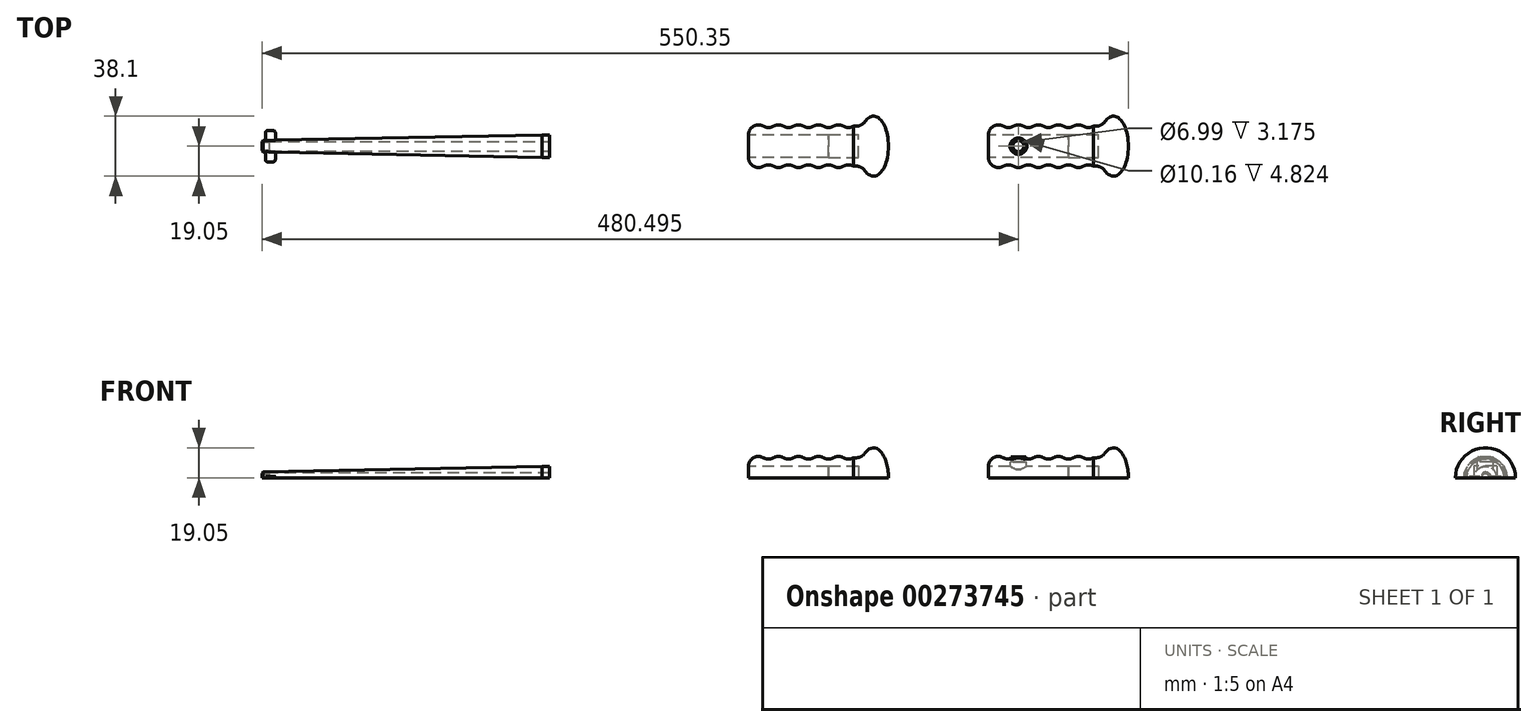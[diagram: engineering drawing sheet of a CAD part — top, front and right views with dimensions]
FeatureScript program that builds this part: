
annotation { "Feature Type Name" : "Feature", "Feature Type Description" : "" }
export const myFeature = defineFeature(function(context is Context, id is Id, definition is map)
    precondition{}
    {
        {
            var Q0;
            Q0=qCreatedBy(makeId("Top.planeOp"),FACE);
            var sketch = newSketch(context, id + "F0", { "sketchPlane" : qUnion([Q0])});
            skPoint(sketch, "E0.middle", {"position": v(0, 0) * mm});
            skEllipticalArc(sketch, "E1", {});
            skPoint(sketch, "E2.orphan", {"position": v(57.15, -12.7) * mm});
            skPoint(sketch, "E3.orphan", {"position": v(57.15, 12.7) * mm});
            skArc(sketch, "E4.3.0.1", {"start": v(-12.7, 12.7) * mm, "mid": v(-9.52, 11.85) * mm, "end": v(-6.35, 12.7) * mm});
            skArc(sketch, "E4.4.0.0", {"start": v(0, 12.7) * mm, "mid": v(-3.17, 13.55) * mm, "end": v(-6.35, 12.7) * mm});
            skArc(sketch, "E4.4.0.1", {"start": v(0, 12.7) * mm, "mid": v(3.18, 11.85) * mm, "end": v(6.35, 12.7) * mm});
            skArc(sketch, "E4.5.0.0", {"start": v(12.7, 12.7) * mm, "mid": v(9.53, 13.55) * mm, "end": v(6.35, 12.7) * mm});
            skArc(sketch, "E4.5.0.1", {"start": v(12.7, 12.7) * mm, "mid": v(15.88, 11.85) * mm, "end": v(19.05, 12.7) * mm});
            skArc(sketch, "E4.6.0.0", {"start": v(25.4, 12.7) * mm, "mid": v(22.23, 13.55) * mm, "end": v(19.05, 12.7) * mm});
            skArc(sketch, "E4.6.0.1", {"start": v(25.4, 12.7) * mm, "mid": v(28.58, 11.85) * mm, "end": v(31.75, 12.7) * mm});
            skArc(sketch, "E4.7.0.0", {"start": v(38.1, 12.7) * mm, "mid": v(34.93, 13.55) * mm, "end": v(31.75, 12.7) * mm});
            skArc(sketch, "E4.7.0.1", {"start": v(38.1, 12.7) * mm, "mid": v(41.28, 11.85) * mm, "end": v(44.45, 12.7) * mm});
            skLineSegment(sketch, "E5", {"start": v(44.45, 12.7) * mm, "end": v(46.35, 12.7) * mm});
            skPoint(sketch, "E6.visualSharp", {"position": v(50.05, 12.7) * mm});
            skArc(sketch, "E6.filletArc", {"start": v(46.35, 12.7) * mm, "mid": v(49.3, 13.43) * mm, "end": v(51.57, 15.44) * mm});
            skLineSegment(sketch, "E7", {"start": v(-22.22, 0) * mm, "end": v(66.68, 0) * mm});
            skLineSegment(sketch, "E8", {"start": v(-22.22, 0) * mm, "end": v(-22.22, 7.2) * mm});
            skArc(sketch, "E9.converted", {"start": v(-12.7, 12.7) * mm, "mid": v(-19.05, 12.7) * mm, "end": v(-22.23, 7.2) * mm});
            skPoint(sketch, "E10.orphan", {"position": v(-19.05, 12.7) * mm});
            const initialGuessF0  = {"E1": [0.05715, 0, 0, 1, 0.01905, 0.009525, 4.71238898038469, 0.6259709660529879]};
            skSetInitialGuess(sketch, initialGuessF0);
            skSolve(sketch);
        }
        {
            var Q0;
            Q0=makeQuery(id+"F0.imprint","IMPRINT",FACE,{"disambiguationData":[TD([[makeQuery(id+"F0.imprint","IMPRINT",EDGE,{"derivedFrom":sQuery(id+"F0.wireOp",EDGE,"E1")}),1.0]])]});
            var Q1;
            Q1=sQuery(id+"F0.wireOp",EDGE,"E7");
            revolve(context, id + "F1", {"entities" : qUnion([Q0]), "axis" : qUnion([Q1]), "revolveType" : RevolveType.ONE_DIRECTION, "angle" : 180 * degree});
        }
        {
            var Q0;
            Q0=makeQuery(id+"F1.opRevolve","SWEPT_FACE",FACE,{"disambiguationData":[OSD([sQuery(id+"F0.wireOp",EDGE,"E8")])]});
            extrude(context, id + "F2", {"entities" : qUnion([Q0]), "operationType" : NewBodyOperationType.REMOVE, "oppositeDirection" : true, "depth" : 50.8 * mm});
        }
        {
            var Q0;
            Q0=qCreatedBy(makeId("Top.planeOp"),FACE);
            var sketch = newSketch(context, id + "F3", { "sketchPlane" : qUnion([Q0])});
            skLineSegment(sketch, "E11", {"start": v(-52.07, 0) * mm, "end": v(-331.27, 0) * mm, "construction": true});
            skPoint(sketch, "E11.endSnap0", {"position": v(-60.33, 0) * mm});
            skLineSegment(sketch, "E12", {"start": v(-331.27, 2.5) * mm, "end": v(-331.27, 3.57) * mm});
            skLineSegment(sketch, "E13", {"start": v(-331.27, 3.57) * mm, "end": v(-153.5, 7.2) * mm});
            skLineSegment(sketch, "E14.0", {"start": v(-148.43, 7.2) * mm, "end": v(-153.5, 7.2) * mm});
            skLineSegment(sketch, "E15", {"start": v(-331.27, 2.5) * mm, "end": v(-326.27, 2.5) * mm});
            skLineSegment(sketch, "E16", {"start": v(-326.27, 2.5) * mm, "end": v(-326.28, 3) * mm});
            skLineSegment(sketch, "E17", {"start": v(-326.28, 3) * mm, "end": v(-148.43, 3) * mm});
            skPoint(sketch, "E18.orphan", {"position": v(-52.07, 0) * mm});
            skLineSegment(sketch, "E19", {"start": v(-148.43, 7.2) * mm, "end": v(-148.43, 3) * mm});
            skSolve(sketch);
        }
        {
            var Q0;
            {var subQ1=sQuery(id+"F3.wireOp",EDGE,"E13");Q0=makeQuery(id+"F3.imprint","IMPRINT",FACE,{"disambiguationData":[TD([[makeQuery(id+"F3.imprint","IMPRINT",EDGE,{"derivedFrom":subQ1}),-1.0]])]});}
            var Q1;
            Q1=sQuery(id+"F3.wireOp",EDGE,"E11");
            revolve(context, id + "F4", {"entities" : qUnion([Q0]), "axis" : qUnion([Q1]), "revolveType" : RevolveType.ONE_DIRECTION, "oppositeDirection" : true, "angle" : 180 * degree});
        }
        {
            var Q0;
            Q0=makeQuery(id+"F4.opRevolve","SWEPT_EDGE",EDGE,{"disambiguationData":[OSD([sQuery(id+"F3.wireOp",EDGE,"E12"),sQuery(id+"F3.wireOp",EDGE,"E13")])]});
            chamfer(context, id + "F5", {"entities" : qUnion([Q0]), "width" : 0.76 * mm, "tangentPropagation" : true});
        }
        {
            var Q0;
            Q0=makeQuery(id+"F4.opRevolve","CAP_FACE",FACE,{"disambiguationData":[OSD([sQuery(id+"F3.wireOp",EDGE,"E12"),sQuery(id+"F3.wireOp",EDGE,"E13"),sQuery(id+"F3.wireOp",EDGE,"E14.0"),sQuery(id+"F3.wireOp",EDGE,"E15"),sQuery(id+"F3.wireOp",EDGE,"E16"),sQuery(id+"F3.wireOp",EDGE,"E17"),sQuery(id+"F3.wireOp",EDGE,"E19")])],"isStart":false});
            var sketch = newSketch(context, id + "F6", { "sketchPlane" : qUnion([Q0])});
            skLineSegment(sketch, "E20", {"start": v(-329, 4) * mm, "end": v(-329.08, 8.44) * mm});
            skLineSegment(sketch, "E21", {"start": v(-327.59, 10) * mm, "end": v(-324.29, 10.06) * mm});
            skLineSegment(sketch, "E22", {"start": v(-322.73, 8.57) * mm, "end": v(-322.64, 4.18) * mm});
            skPoint(sketch, "E23.visualSharp", {"position": v(-329.11, 9.96) * mm});
            skArc(sketch, "E23.filletArc", {"start": v(-327.59, 10) * mm, "mid": v(-328.66, 9.52) * mm, "end": v(-329.08, 8.44) * mm});
            skPoint(sketch, "E24.visualSharp", {"position": v(-322.76, 10.1) * mm});
            skArc(sketch, "E24.filletArc", {"start": v(-322.73, 8.57) * mm, "mid": v(-323.2, 9.64) * mm, "end": v(-324.29, 10.06) * mm});
            skPoint(sketch, "E25.visualSharp", {"position": v(-322.63, 3.74) * mm});
            skArc(sketch, "E25.filletArc", {"start": v(-323.02, 3.79) * mm, "mid": v(-322.75, 3.9) * mm, "end": v(-322.64, 4.18) * mm});
            skPoint(sketch, "E26.visualSharp", {"position": v(-328.98, 3.61) * mm});
            skArc(sketch, "E26.filletArc", {"start": v(-329, 4) * mm, "mid": v(-328.87, 3.73) * mm, "end": v(-328.6, 3.62) * mm});
            skLineSegment(sketch, "E27.0", {"start": v(-331.27, 2.5) * mm, "end": v(-326.27, 2.5) * mm});
            skLineSegment(sketch, "E28.0.0", {"start": v(-326.27, 2.5) * mm, "end": v(-326.27, -2.5) * mm, "construction": true});
            skLineSegment(sketch, "E28.0.1", {"start": v(-326.27, 2.5) * mm, "end": v(-331.27, 2.5) * mm, "construction": true});
            skLineSegment(sketch, "E28.0.2", {"start": v(-331.27, -2.5) * mm, "end": v(-331.27, 2.5) * mm, "construction": true});
            skLineSegment(sketch, "E28.0.3", {"start": v(-331.27, -2.5) * mm, "end": v(-326.27, -2.5) * mm, "construction": true});
            skLineSegment(sketch, "E29", {"start": v(-331.27, 0) * mm, "end": v(-326.27, 0) * mm, "construction": true});
            skLineSegment(sketch, "E30.MirrorCS", {"start": v(-329, -4) * mm, "end": v(-329.08, -8.44) * mm});
            skArc(sketch, "E31.MirrorCS", {"start": v(-327.59, -10) * mm, "mid": v(-328.66, -9.52) * mm, "end": v(-329.08, -8.44) * mm});
            skLineSegment(sketch, "E32.MirrorCS", {"start": v(-327.59, -10) * mm, "end": v(-324.29, -10.06) * mm});
            skArc(sketch, "E33.MirrorCS", {"start": v(-322.73, -8.57) * mm, "mid": v(-323.2, -9.64) * mm, "end": v(-324.29, -10.06) * mm});
            skLineSegment(sketch, "E34.MirrorCS", {"start": v(-322.73, -8.57) * mm, "end": v(-322.64, -4.18) * mm});
            skArc(sketch, "E35.MirrorCS", {"start": v(-323.02, -3.79) * mm, "mid": v(-322.75, -3.9) * mm, "end": v(-322.64, -4.18) * mm});
            skArc(sketch, "E36.MirrorCS", {"start": v(-329, -4) * mm, "mid": v(-328.87, -3.73) * mm, "end": v(-328.6, -3.62) * mm});
            skLineSegment(sketch, "E37", {"start": v(-328.6, 3.62) * mm, "end": v(-328.6, 3.37) * mm});
            skLineSegment(sketch, "E38", {"start": v(-328.6, 3.37) * mm, "end": v(-323.02, 3.48) * mm});
            skLineSegment(sketch, "E39", {"start": v(-323.02, 3.48) * mm, "end": v(-323.02, 3.79) * mm});
            skLineSegment(sketch, "E40.MirrorCS", {"start": v(-328.6, 3.37) * mm, "end": v(-334.18, 3.25) * mm});
            skLineSegment(sketch, "E41.MirrorCS", {"start": v(-328.6, -3.62) * mm, "end": v(-328.6, -3.37) * mm});
            skLineSegment(sketch, "E42.MirrorCS", {"start": v(-328.6, -3.37) * mm, "end": v(-323.02, -3.48) * mm});
            skLineSegment(sketch, "E43.MirrorCS", {"start": v(-323.02, -3.48) * mm, "end": v(-323.02, -3.79) * mm});
            skSolve(sketch);
        }
        {
            var Q0;
            Q0=makeQuery(id+"F6.imprint","IMPRINT",FACE,{"disambiguationData":[TD([[makeQuery(id+"F6.imprint","IMPRINT",EDGE,{"derivedFrom":sQuery(id+"F6.wireOp",EDGE,"E30.MirrorCS")}),1.0]])]});
            var Q1;
            Q1=makeQuery(id+"F6.imprint","IMPRINT",FACE,{"disambiguationData":[TD([[makeQuery(id+"F6.imprint","IMPRINT",EDGE,{"derivedFrom":sQuery(id+"F6.wireOp",EDGE,"E20")}),-1.0]])]});
            var Q2;
            {var subQ0=sQuery(id+"F6.wireOp",EDGE,"E37");Q2=makeQuery(id+"F6.imprint","IMPRINT",FACE,{"disambiguationData":[TD([[makeQuery(id+"F6.imprint","IMPRINT",EDGE,{"derivedFrom":subQ0}),1.0]])]});}
            extrude(context, id + "F7", {"entities" : qUnion([Q0, Q1, Q2]), "operationType" : NewBodyOperationType.ADD, "oppositeDirection" : true, "depth" : 0.76 * mm});
        }
        {
            var Q0;
            Q0=makeQuery(id+"F1.opRevolve","CAP_FACE",FACE,{"disambiguationData":[OSD([sQuery(id+"F0.wireOp",EDGE,"E1"),sQuery(id+"F0.wireOp",EDGE,"E4.3.0.1"),sQuery(id+"F0.wireOp",EDGE,"E4.4.0.0"),sQuery(id+"F0.wireOp",EDGE,"E4.4.0.1"),sQuery(id+"F0.wireOp",EDGE,"E4.5.0.0"),sQuery(id+"F0.wireOp",EDGE,"E4.5.0.1"),sQuery(id+"F0.wireOp",EDGE,"E4.6.0.0"),sQuery(id+"F0.wireOp",EDGE,"E4.6.0.1"),sQuery(id+"F0.wireOp",EDGE,"E4.7.0.0"),sQuery(id+"F0.wireOp",EDGE,"E4.7.0.1"),sQuery(id+"F0.wireOp",EDGE,"E5"),sQuery(id+"F0.wireOp",EDGE,"E6.filletArc"),sQuery(id+"F0.wireOp",EDGE,"E7"),sQuery(id+"F0.wireOp",EDGE,"E8"),sQuery(id+"F0.wireOp",EDGE,"E9.converted")])],"isStart":true});
            var sketch = newSketch(context, id + "F8", { "sketchPlane" : qUnion([Q0])});
            skLineSegment(sketch, "E44.bottom", {"start": v(28.58, 7.3) * mm, "end": v(47.63, 7.3) * mm});
            skLineSegment(sketch, "E44.top", {"start": v(28.58, -7.3) * mm, "end": v(47.63, -7.3) * mm});
            skLineSegment(sketch, "E44.left", {"start": v(28.58, 7.3) * mm, "end": v(28.58, -7.3) * mm});
            skLineSegment(sketch, "E44.right", {"start": v(47.63, 7.3) * mm, "end": v(47.63, -7.3) * mm});
            skLineSegment(sketch, "E45.0", {"start": v(28.58, -7.2) * mm, "end": v(28.58, 7.2) * mm, "construction": true});
            skLineSegment(sketch, "E46", {"start": v(28.58, 0) * mm, "end": v(24.41, 0) * mm, "construction": true});
            skPoint(sketch, "E46.endSnap0", {"position": v(28.58, 0) * mm});
            skSolve(sketch);
        }
        {
            var Q0;
            Q0=makeQuery(id+"F8.imprint","IMPRINT",FACE,{"disambiguationData":[TD([[makeQuery(id+"F8.imprint","IMPRINT",EDGE,{"derivedFrom":sQuery(id+"F8.wireOp",EDGE,"E44.bottom")}),-1.0]])]});
            extrude(context, id + "F9", {"entities" : qUnion([Q0]), "operationType" : NewBodyOperationType.REMOVE, "oppositeDirection" : true, "depth" : 7.37 * mm});
        }
        {
            var Q0;
            Q0=makeQuery(id+"F1.opRevolve","SWEPT_BODY",BODY,{"disambiguationData":[OSD([sQuery(id+"F0.wireOp",EDGE,"E1"),sQuery(id+"F0.wireOp",EDGE,"E4.3.0.1"),sQuery(id+"F0.wireOp",EDGE,"E4.4.0.0"),sQuery(id+"F0.wireOp",EDGE,"E4.4.0.1"),sQuery(id+"F0.wireOp",EDGE,"E4.5.0.0"),sQuery(id+"F0.wireOp",EDGE,"E4.5.0.1"),sQuery(id+"F0.wireOp",EDGE,"E4.6.0.0"),sQuery(id+"F0.wireOp",EDGE,"E4.6.0.1"),sQuery(id+"F0.wireOp",EDGE,"E4.7.0.0"),sQuery(id+"F0.wireOp",EDGE,"E4.7.0.1"),sQuery(id+"F0.wireOp",EDGE,"E5"),sQuery(id+"F0.wireOp",EDGE,"E6.filletArc"),sQuery(id+"F0.wireOp",EDGE,"E7"),sQuery(id+"F0.wireOp",EDGE,"E8"),sQuery(id+"F0.wireOp",EDGE,"E9.converted")])]});
            transform(context, id + "F10", {"entities" : qUnion([Q0]), "transformType" : TransformType.TRANSLATION_3D, "dx" : 152.4 * mm, "dy" : 0 * mm, "dz" : 0 * mm, "makeCopy" : true});
        }
        {
            var Q0;
            Q0=makeQuery(id+"F10.opPattern","COPY",FACE,{"derivedFrom":makeQuery(id+"F1.opRevolve","CAP_FACE",FACE,{"disambiguationData":[OSD([sQuery(id+"F0.wireOp",EDGE,"E1"),sQuery(id+"F0.wireOp",EDGE,"E4.3.0.1"),sQuery(id+"F0.wireOp",EDGE,"E4.4.0.0"),sQuery(id+"F0.wireOp",EDGE,"E4.4.0.1"),sQuery(id+"F0.wireOp",EDGE,"E4.5.0.0"),sQuery(id+"F0.wireOp",EDGE,"E4.5.0.1"),sQuery(id+"F0.wireOp",EDGE,"E4.6.0.0"),sQuery(id+"F0.wireOp",EDGE,"E4.6.0.1"),sQuery(id+"F0.wireOp",EDGE,"E4.7.0.0"),sQuery(id+"F0.wireOp",EDGE,"E4.7.0.1"),sQuery(id+"F0.wireOp",EDGE,"E5"),sQuery(id+"F0.wireOp",EDGE,"E6.filletArc"),sQuery(id+"F0.wireOp",EDGE,"E7"),sQuery(id+"F0.wireOp",EDGE,"E8"),sQuery(id+"F0.wireOp",EDGE,"E9.converted")])],"isStart":true}),"instanceName":"1"});
            var sketch = newSketch(context, id + "F11", { "sketchPlane" : qUnion([Q0])});
            skLineSegment(sketch, "E47", {"start": v(149.23, -13.55) * mm, "end": v(149.23, 13.55) * mm, "construction": true});
            skCircle(sketch, "E48", {"center": v(149.23, 0) * mm, "radius": 3.5 * mm});
            skSolve(sketch);
        }
        {
            var Q0;
            Q0 = qSketchRegion(id + "F11", true);
            extrude(context, id + "F12", {"entities" : qUnion([Q0]), "operationType" : NewBodyOperationType.REMOVE, "oppositeDirection" : true, "depth" : 25.4 * mm});
        }
        {
            var Q0;
            Q0=makeQuery(id+"F12.boolean.opBoolean","INTERSECT",EDGE,{"disambiguationData":[OD(1.0)],"derivedFrom":[makeQuery(id+"F10.opPattern","COPY",FACE,{"derivedFrom":makeQuery(id+"F1.opRevolve","SWEPT_FACE",FACE,{"disambiguationData":[OSD([sQuery(id+"F0.wireOp",EDGE,"E4.4.0.0")])]}),"instanceName":"1"}),makeQuery(id+"F12.opExtrude","SWEPT_FACE",FACE,{"disambiguationData":[OSD([sQuery(id+"F11.wireOp",EDGE,"E48")])]})]});
            cPoint(context, id + "F13", {"entities" : qUnion([Q0]), "parameter" : 0.5});
        }
        {
            var Q0;
            Q0=makeQuery(id+"F10.opPattern","COPY",FACE,{"derivedFrom":makeQuery(id+"F1.opRevolve","CAP_FACE",FACE,{"disambiguationData":[OSD([sQuery(id+"F0.wireOp",EDGE,"E1"),sQuery(id+"F0.wireOp",EDGE,"E4.3.0.1"),sQuery(id+"F0.wireOp",EDGE,"E4.4.0.0"),sQuery(id+"F0.wireOp",EDGE,"E4.4.0.1"),sQuery(id+"F0.wireOp",EDGE,"E4.5.0.0"),sQuery(id+"F0.wireOp",EDGE,"E4.5.0.1"),sQuery(id+"F0.wireOp",EDGE,"E4.6.0.0"),sQuery(id+"F0.wireOp",EDGE,"E4.6.0.1"),sQuery(id+"F0.wireOp",EDGE,"E4.7.0.0"),sQuery(id+"F0.wireOp",EDGE,"E4.7.0.1"),sQuery(id+"F0.wireOp",EDGE,"E5"),sQuery(id+"F0.wireOp",EDGE,"E6.filletArc"),sQuery(id+"F0.wireOp",EDGE,"E7"),sQuery(id+"F0.wireOp",EDGE,"E8"),sQuery(id+"F0.wireOp",EDGE,"E9.converted")])],"isStart":true}),"instanceName":"1"});
            var Q1;
            Q1 = qCreatedBy(id + "F13" ,VERTEX);
            cPlane(context, id + "F14", {"entities" : qUnion([Q0, Q1]), "cplaneType" : CPlaneType.PLANE_POINT, "offset" : 25.4 * mm, "width" : 152.4 * mm, "height" : 152.4 * mm});
        }
        {
            var Q0;
            Q0=qCreatedBy(id+"F14.planeOp",FACE);
            var sketch = newSketch(context, id + "F15", { "sketchPlane" : qUnion([Q0])});
            skPoint(sketch, "E49.0", {"position": v(149.22, 3.5) * mm});
            skPoint(sketch, "E50.0", {"position": v(149.23, -3.5) * mm});
            skLineSegment(sketch, "E51", {"start": v(149.22, 3.5) * mm, "end": v(149.23, -3.5) * mm, "construction": true});
            skCircle(sketch, "E52", {"center": v(149.22, 0) * mm, "radius": 4.76 * mm});
            skCircle(sketch, "E53", {"center": v(149.22, 0) * mm, "radius": 3.5 * mm});
            skSolve(sketch);
        }
        {
            var Q0;
            Q0=makeQuery(id+"F15.imprint","IMPRINT",FACE,{"disambiguationData":[TD([[makeQuery(id+"F15.imprint","IMPRINT",EDGE,{"derivedFrom":sQuery(id+"F15.wireOp",EDGE,"E52")}),1.0]])]});
            var Q1;
            Q1=makeQuery(id+"F10.opPattern","COPY",BODY,{"derivedFrom":makeQuery(id+"F1.opRevolve","SWEPT_BODY",BODY,{"disambiguationData":[OSD([sQuery(id+"F0.wireOp",EDGE,"E1"),sQuery(id+"F0.wireOp",EDGE,"E4.3.0.1"),sQuery(id+"F0.wireOp",EDGE,"E4.4.0.0"),sQuery(id+"F0.wireOp",EDGE,"E4.4.0.1"),sQuery(id+"F0.wireOp",EDGE,"E4.5.0.0"),sQuery(id+"F0.wireOp",EDGE,"E4.5.0.1"),sQuery(id+"F0.wireOp",EDGE,"E4.6.0.0"),sQuery(id+"F0.wireOp",EDGE,"E4.6.0.1"),sQuery(id+"F0.wireOp",EDGE,"E4.7.0.0"),sQuery(id+"F0.wireOp",EDGE,"E4.7.0.1"),sQuery(id+"F0.wireOp",EDGE,"E5"),sQuery(id+"F0.wireOp",EDGE,"E6.filletArc"),sQuery(id+"F0.wireOp",EDGE,"E7"),sQuery(id+"F0.wireOp",EDGE,"E8"),sQuery(id+"F0.wireOp",EDGE,"E9.converted")])]}),"instanceName":"1"});
            extrude(context, id + "F16", {"entities" : qUnion([Q0]), "operationType" : NewBodyOperationType.ADD, "endBound" : BoundingType.UP_TO_BODY, "endBoundEntityBody" : qUnion([Q1]), "depth" : 25.4 * mm});
        }
        {
            var Q0;
            Q0=makeQuery(id+"F16.boolean.opBoolean","INTERSECT",EDGE,{"derivedFrom":[makeQuery(id+"F12.boolean.opBoolean","SPLIT",FACE,{"disambiguationData":[OD(1.0)],"derivedFrom":makeQuery(id+"F10.opPattern","COPY",FACE,{"derivedFrom":makeQuery(id+"F1.opRevolve","SWEPT_FACE",FACE,{"disambiguationData":[OSD([sQuery(id+"F0.wireOp",EDGE,"E4.4.0.0")])]}),"instanceName":"1"})}),makeQuery(id+"F16.opExtrude","SWEPT_FACE",FACE,{"disambiguationData":[OSD([sQuery(id+"F15.wireOp",EDGE,"E52")])]})]});
            var Q1;
            Q1=makeQuery(id+"F16.boolean.opBoolean","INTERSECT",EDGE,{"disambiguationData":[OD(0.0)],"derivedFrom":[makeQuery(id+"F10.opPattern","COPY",FACE,{"derivedFrom":makeQuery(id+"F1.opRevolve","SWEPT_FACE",FACE,{"disambiguationData":[OSD([sQuery(id+"F0.wireOp",EDGE,"E4.4.0.1")])]}),"instanceName":"1"}),makeQuery(id+"F16.opExtrude","SWEPT_FACE",FACE,{"disambiguationData":[OSD([sQuery(id+"F15.wireOp",EDGE,"E52")])]})]});
            fillet(context, id + "F17", {"entities" : qUnion([Q0, Q1]), "radius" : 0.76 * mm, "tangentPropagation" : true, "allowEdgeOverflow" : false});
        }
        {
            var Q0;
            Q0=qCreatedBy(id+"F14.planeOp",FACE);
            cPlane(context, id + "F18", {"entities" : qUnion([Q0]), "cplaneType" : CPlaneType.OFFSET, "offset" : 3.17 * mm, "width" : 152.4 * mm, "height" : 152.4 * mm});
        }
        {
            var Q0;
            Q0=qCreatedBy(id+"F18.planeOp",FACE);
            var sketch = newSketch(context, id + "F19", { "sketchPlane" : qUnion([Q0])});
            skCircle(sketch, "E54.0", {"center": v(149.23, 0) * mm, "radius": 3.5 * mm});
            skCircle(sketch, "E55", {"center": v(149.23, 0) * mm, "radius": 5.08 * mm});
            skSolve(sketch);
        }
        {
            var Q0;
            Q0=makeQuery(id+"F19.imprint","IMPRINT",FACE,{"disambiguationData":[TD([[makeQuery(id+"F19.imprint","IMPRINT",EDGE,{"derivedFrom":sQuery(id+"F19.wireOp",EDGE,"E54.0")}),-1.0]])]});
            extrude(context, id + "F20", {"entities" : qUnion([Q0]), "operationType" : NewBodyOperationType.REMOVE, "depth" : 12.7 * mm});
        }
    });
